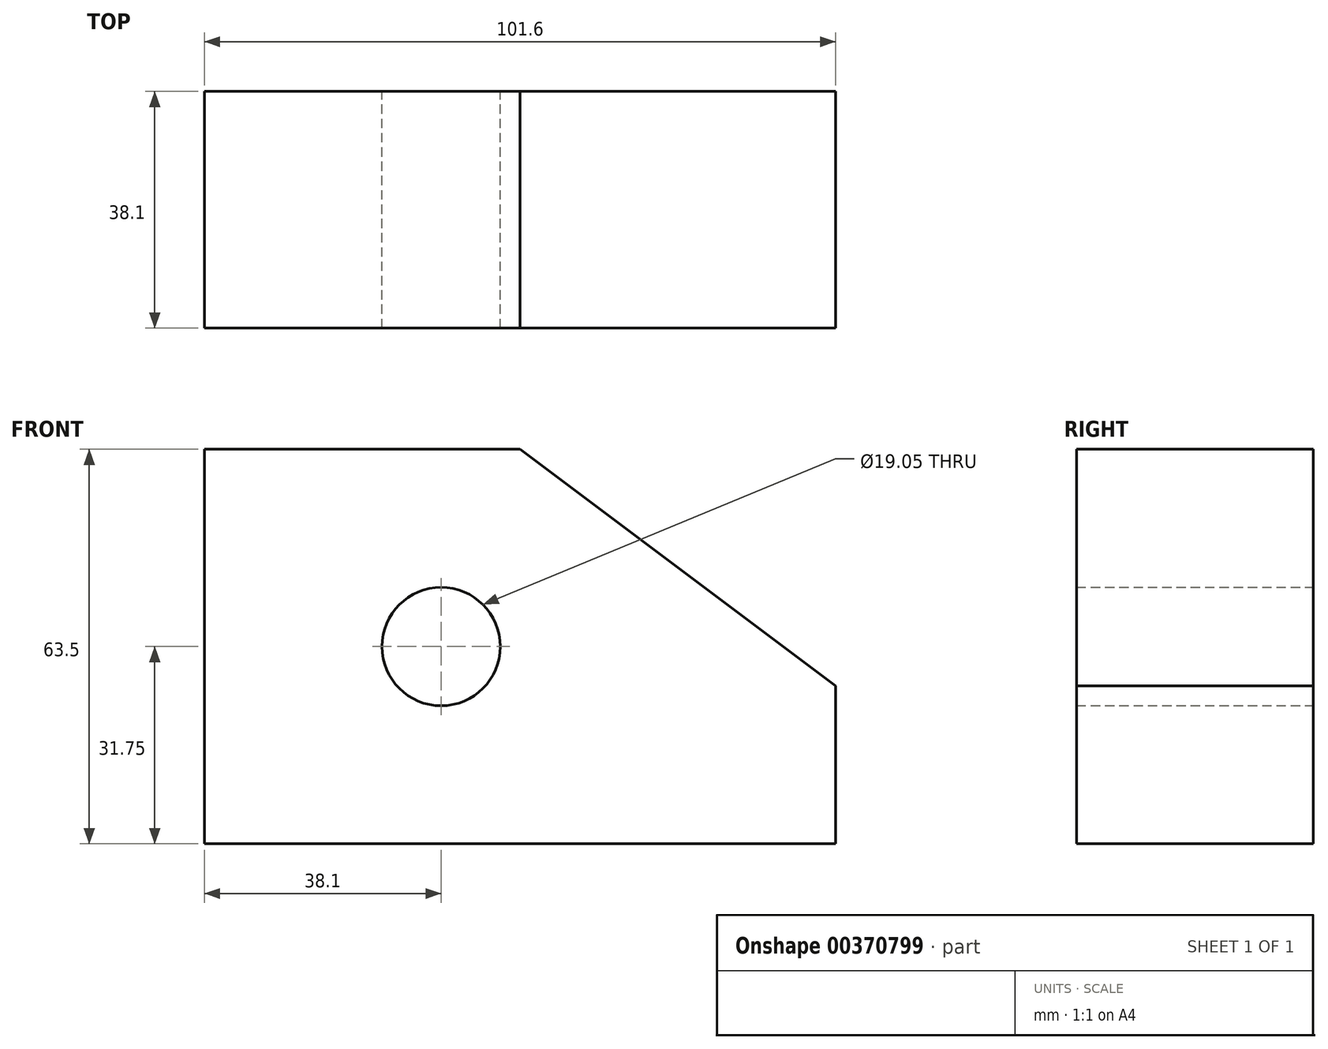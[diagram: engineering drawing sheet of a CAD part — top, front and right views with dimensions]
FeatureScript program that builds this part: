
annotation { "Feature Type Name" : "Feature", "Feature Type Description" : "" }
export const myFeature = defineFeature(function(context is Context, id is Id, definition is map)
    precondition{}
    {
        {
            var Q0;
            Q0=qCreatedBy(makeId("Front.planeOp"),FACE);
            var sketch = newSketch(context, id + "F0", { "sketchPlane" : qUnion([Q0])});
            skLineSegment(sketch, "E0", {"start": v(0, 0) * mm, "end": v(0, 63.5) * mm});
            skLineSegment(sketch, "E1", {"start": v(0, 63.5) * mm, "end": v(50.8, 63.5) * mm});
            skLineSegment(sketch, "E2", {"start": v(50.8, 63.5) * mm, "end": v(101.6, 25.4) * mm});
            skLineSegment(sketch, "E3", {"start": v(101.6, 25.4) * mm, "end": v(101.6, 0) * mm});
            skLineSegment(sketch, "E4", {"start": v(101.6, 0) * mm, "end": v(0, 0) * mm});
            skCircle(sketch, "E5", {"center": v(38.1, 31.75) * mm, "radius": 9.53 * mm});
            skSolve(sketch);
        }
        {
            var Q0;
            Q0 = qSketchRegion(id + "F0", true);
            extrude(context, id + "F1", {"entities" : qUnion([Q0]), "depth" : 38.1 * mm});
        }
    });
